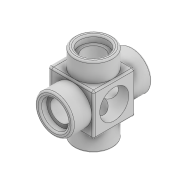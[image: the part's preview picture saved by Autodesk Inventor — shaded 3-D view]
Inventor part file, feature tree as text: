
AUTODESK INVENTOR PART (.ipt)
format: ipt  version: 2020 (Build 240168000, 168)  size: 289,792 bytes
history: native  units: mm
features: extrude x11, sketch x11, fillet x3, mirror x2, plane x1, projected_geometry x1
ambient origin geometry x8: Origin, YZ Plane, XZ Plane, XY Plane, X Axis, Y Axis, Z Axis, Center Point
bodies: Solid1 (feature_tree)
feature tree (29):
  extrude  "Extrusion1"  Depth=6.0mm
  extrude  "Extrusion2"  Depth=5.5mm
  extrude  "Extrusion3"  Depth=5.5mm
  extrude  "Extrusion4"  Depth=5.5mm
  extrude  "Extrusion5"  Depth=5.5mm
  extrude  "Extrusion7"  Depth=3.0mm
  extrude  "Extrusion8"  Depth=3.0mm
  extrude  "Extrusion9"  Depth=4.0mm
  extrude  "Extrusion10"  Depth=4.0mm
  mirror  "Mirror1"
  mirror  "Mirror2"
  extrude  "Extrusion11"  Depth=1.0mm TaperAngle=0.0deg
  extrude  "Extrusion12"  Depth=5.5mm TaperAngle=0.0deg
  fillet  "Fillet4"  Radius=0.25mm
  fillet  "Fillet5"  Radius=0.25mm
  fillet  "Fillet6"  Radius=1.0mm
  sketch  "Sketch1"  dims[d0=6.0mm d1=6.0mm]
  sketch  "Sketch2"  dims[d2=6.0mm d3=0.0mm d4=5.5mm]
  sketch  "Sketch3"  dims[d5=2.75mm d6=0.0mm d7=5.5mm]
  sketch  "Sketch4"  dims[d8=2.75mm d9=0.0mm d10=5.5mm]
  sketch  "Sketch5"  dims[d11=2.75mm d12=0.0mm d13=5.5mm]
  sketch  "Sketch8"  dims[d14=2.75mm d15=0.0mm d23=3.0mm]
  sketch  "Sketch9"  dims[d24=0.0mm d25=0.0mm d26=3.0mm]
  sketch  "Sketch10"  dims[d27=0.0mm d28=0.0mm d30=4.0mm]
  sketch  "Sketch11"  dims[d31=1.0mm d32=0.0mm d33=4.0mm]
  plane  "Work Plane1"
  sketch  "Sketch12"  dims[d34=1.0mm d35=0.0mm d36=1.0mm d37=0.0mm]
  projected_geometry  "Projected Loop1"
  sketch  "Sketch13"  dims[d38=4.2mm d39=5.5mm d40=0.0mm d41=0.25mm d42=0.25mm d43=1.0mm]
